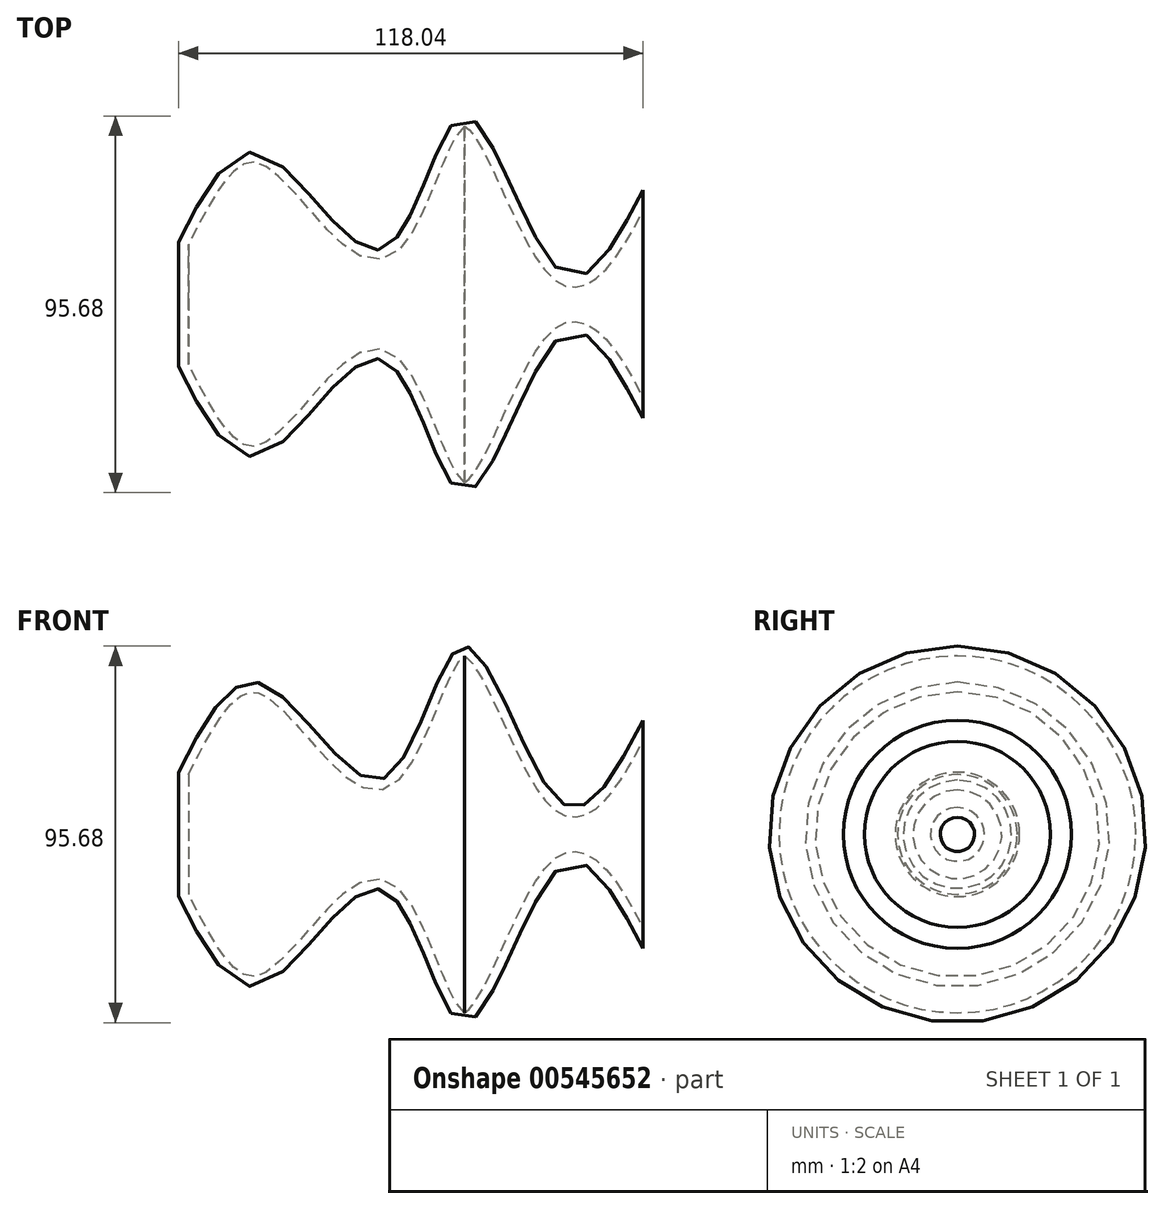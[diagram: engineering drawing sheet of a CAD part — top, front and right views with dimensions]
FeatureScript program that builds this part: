
annotation { "Feature Type Name" : "Feature", "Feature Type Description" : "" }
export const myFeature = defineFeature(function(context is Context, id is Id, definition is map)
    precondition{}
    {
        {
            var Q0;
            Q0=qCreatedBy(makeId("Front.planeOp"),FACE);
            var sketch = newSketch(context, id + "F0", { "sketchPlane" : qUnion([Q0])});
            skFitSpline(sketch, "E0", {"points": [v(-63.19, 15.8) * mm, v(-41.69, 38.18) * mm, v(-11.4, 14.04) * mm, v(9.21, 47.83) * mm, v(34.23, 7.9) * mm, v(54.85, 28.96) * mm], "startDerivative": vector(106.06, 209.28) * mm, "endDerivative": vector(114.77, 217.26) * mm});
            skLineSegment(sketch, "E1", {"start": v(-63.19, 15.8) * mm, "end": v(-63.19, 0) * mm});
            skLineSegment(sketch, "E2", {"start": v(-63.19, 0) * mm, "end": v(54.85, 0) * mm});
            skLineSegment(sketch, "E3", {"start": v(54.85, 0) * mm, "end": v(54.85, 28.96) * mm});
            skSolve(sketch);
        }
        {
            var Q0;
            Q0=makeQuery(id+"F0.imprint","IMPRINT",FACE,{"disambiguationData":[TD([[makeQuery(id+"F0.imprint","IMPRINT",EDGE,{"derivedFrom":sQuery(id+"F0.wireOp",EDGE,"E0")}),-1.0]])]});
            var Q1;
            Q1=sQuery(id+"F0.wireOp",EDGE,"E2");
            revolve(context, id + "F1", {"entities" : qUnion([Q0]), "axis" : qUnion([Q1]), "revolveType" : RevolveType.FULL});
        }
        {
            var Q0;
            Q0=makeQuery(id+"F1.opRevolve","SWEPT_FACE",FACE,{"disambiguationData":[OSD([sQuery(id+"F0.wireOp",EDGE,"E3")])]});
            shell(context, id + "F2", {"entities" : qUnion([Q0]), "thickness" : 2.5 * mm});
        }
    });
